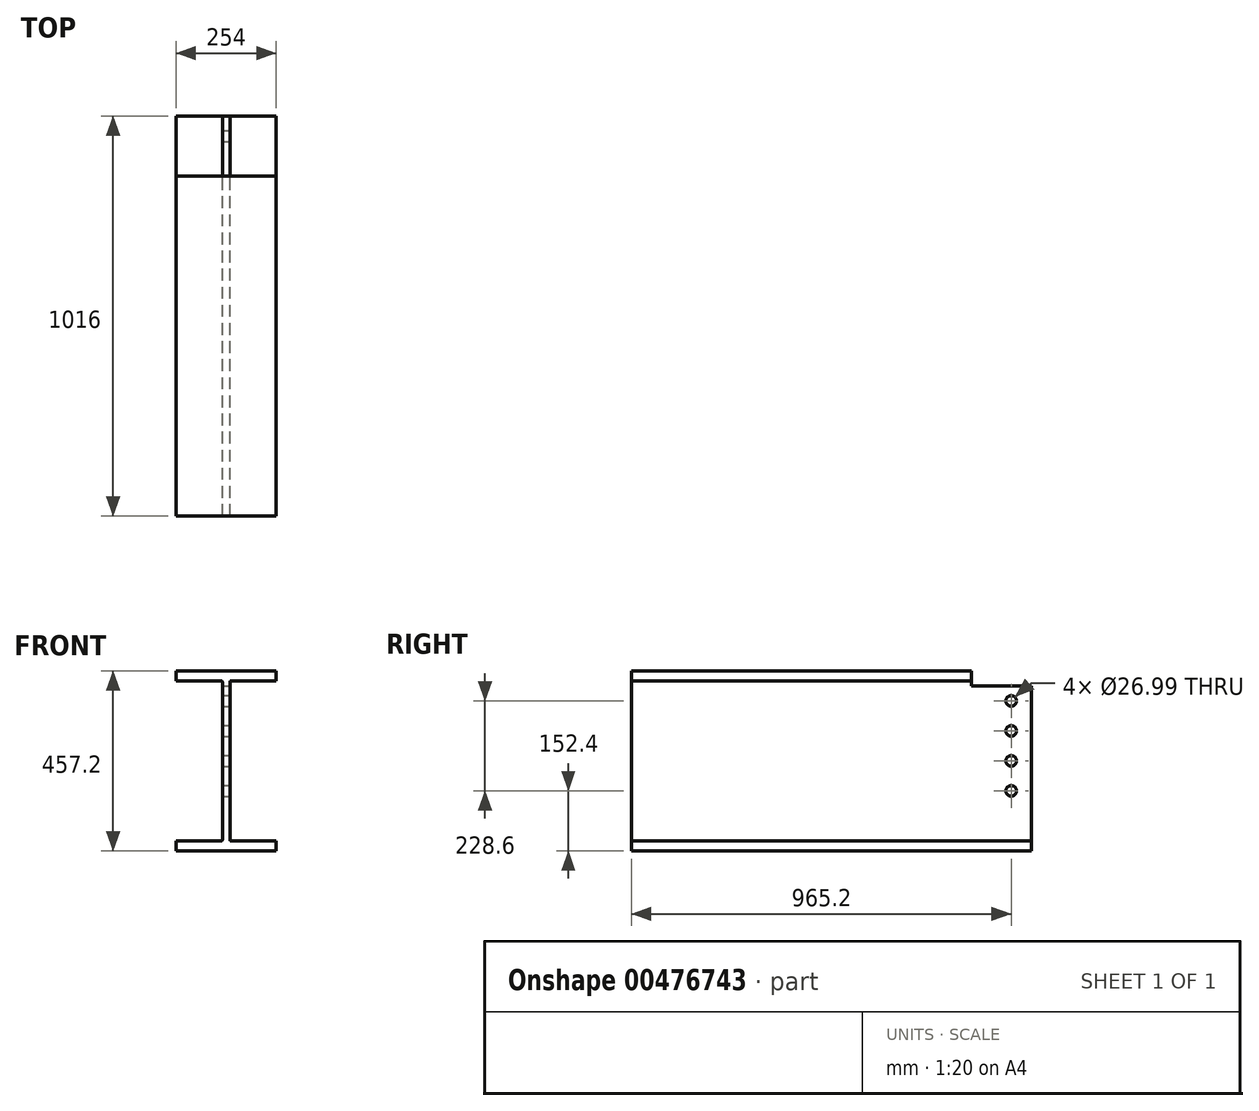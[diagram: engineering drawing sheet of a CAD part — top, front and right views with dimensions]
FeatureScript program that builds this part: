
annotation { "Feature Type Name" : "Feature", "Feature Type Description" : "" }
export const myFeature = defineFeature(function(context is Context, id is Id, definition is map)
    precondition{}
    {
        {
            var Q0;
            Q0=qCreatedBy(makeId("Front.planeOp"),FACE);
            var sketch = newSketch(context, id + "F0", { "sketchPlane" : qUnion([Q0])});
            skLineSegment(sketch, "E0", {"start": v(127, -203.2) * mm, "end": v(12.06, -203.2) * mm});
            skLineSegment(sketch, "E1", {"start": v(9.52, -200.66) * mm, "end": v(9.52, 200.66) * mm});
            skLineSegment(sketch, "E2", {"start": v(12.06, 203.2) * mm, "end": v(127, 203.2) * mm});
            skLineSegment(sketch, "E3", {"start": v(-127, 203.2) * mm, "end": v(-12.06, 203.2) * mm});
            skLineSegment(sketch, "E4", {"start": v(-9.53, 200.66) * mm, "end": v(-9.53, -200.66) * mm});
            skLineSegment(sketch, "E5", {"start": v(-12.06, -203.2) * mm, "end": v(-127, -203.2) * mm});
            skLineSegment(sketch, "E6", {"start": v(0, 0) * mm, "end": v(-9.52, 0) * mm, "construction": true});
            skLineSegment(sketch, "E7", {"start": v(0, 0) * mm, "end": v(9.52, 0) * mm, "construction": true});
            skLineSegment(sketch, "E8", {"start": v(0, 0) * mm, "end": v(0, 228.6) * mm, "construction": true});
            skLineSegment(sketch, "E9", {"start": v(0, 0) * mm, "end": v(0, -228.6) * mm, "construction": true});
            skPoint(sketch, "E10.visualSharp", {"position": v(-9.53, 203.2) * mm});
            skArc(sketch, "E10.filletArc", {"start": v(-9.52, 200.66) * mm, "mid": v(-10.27, 202.46) * mm, "end": v(-12.06, 203.2) * mm});
            skPoint(sketch, "E11.visualSharp", {"position": v(9.53, 203.2) * mm});
            skArc(sketch, "E11.filletArc", {"start": v(12.06, 203.2) * mm, "mid": v(10.27, 202.46) * mm, "end": v(9.52, 200.66) * mm});
            skPoint(sketch, "E12.visualSharp", {"position": v(9.53, -203.2) * mm});
            skArc(sketch, "E12.filletArc", {"start": v(9.52, -200.66) * mm, "mid": v(10.27, -202.46) * mm, "end": v(12.06, -203.2) * mm});
            skPoint(sketch, "E13.visualSharp", {"position": v(-9.53, -203.2) * mm});
            skArc(sketch, "E13.filletArc", {"start": v(-12.06, -203.2) * mm, "mid": v(-10.27, -202.46) * mm, "end": v(-9.52, -200.66) * mm});
            skPoint(sketch, "E14.visualSharp", {"position": v(-127, 228.6) * mm});
            skPoint(sketch, "E15.visualSharp", {"position": v(127, 228.6) * mm});
            skPoint(sketch, "E16.visualSharp", {"position": v(127, 203.2) * mm});
            skPoint(sketch, "E17.visualSharp", {"position": v(127, -228.6) * mm});
            skPoint(sketch, "E18.visualSharp", {"position": v(-127, -203.2) * mm});
            skPoint(sketch, "E19.visualSharp", {"position": v(-127, -228.6) * mm});
            skLineSegment(sketch, "E20", {"start": v(127, -203.2) * mm, "end": v(127, -228.6) * mm});
            skLineSegment(sketch, "E21", {"start": v(-127, -203.2) * mm, "end": v(-127, -228.6) * mm});
            skLineSegment(sketch, "E22", {"start": v(-127, 228.6) * mm, "end": v(-127, 203.2) * mm});
            skLineSegment(sketch, "E23", {"start": v(127, 228.6) * mm, "end": v(127, 203.2) * mm});
            skLineSegment(sketch, "E24", {"start": v(-127, 228.6) * mm, "end": v(127, 228.6) * mm});
            skLineSegment(sketch, "E25", {"start": v(-127, -228.6) * mm, "end": v(127, -228.6) * mm});
            skSolve(sketch);
        }
        {
            var Q0;
            Q0=makeQuery(id+"F0.imprint","IMPRINT",FACE,{"disambiguationData":[TD([[makeQuery(id+"F0.imprint","IMPRINT",EDGE,{"derivedFrom":sQuery(id+"F0.wireOp",EDGE,"E0")}),1.0]])]});
            extrude(context, id + "F1", {"entities" : qUnion([Q0]), "endBound" : BoundingType.SYMMETRIC, "depth" : 1016 * mm});
        }
        {
            var Q0;
            Q0=makeQuery(id+"F1.opExtrude","SWEPT_FACE",FACE,{"disambiguationData":[OSD([sQuery(id+"F0.wireOp",EDGE,"E1")])]});
            var sketch = newSketch(context, id + "F2", { "sketchPlane" : qUnion([Q0])});
            skPoint(sketch, "E26", {"position": v(457.2, 152.4) * mm});
            skPoint(sketch, "E27", {"position": v(457.2, 76.2) * mm});
            skPoint(sketch, "E28", {"position": v(457.2, 0) * mm});
            skPoint(sketch, "E29", {"position": v(457.2, -76.2) * mm});
            skSolve(sketch);
        }
        {
            var Q0;
            Q0=sQuery(id+"F2.wireOp",VERTEX,"E26");
            var Q1;
            Q1=sQuery(id+"F2.wireOp",VERTEX,"E27");
            var Q2;
            Q2=sQuery(id+"F2.wireOp",VERTEX,"E28");
            var Q3;
            Q3=sQuery(id+"F2.wireOp",VERTEX,"E29");
            var Q4;
            Q4=makeQuery(id+"F1.opExtrude","SWEPT_BODY",BODY,{"disambiguationData":[OSD([sQuery(id+"F0.wireOp",EDGE,"E0"),sQuery(id+"F0.wireOp",EDGE,"E1"),sQuery(id+"F0.wireOp",EDGE,"E2"),sQuery(id+"F0.wireOp",EDGE,"E3"),sQuery(id+"F0.wireOp",EDGE,"E4"),sQuery(id+"F0.wireOp",EDGE,"E5"),sQuery(id+"F0.wireOp",EDGE,"E10.filletArc"),sQuery(id+"F0.wireOp",EDGE,"E11.filletArc"),sQuery(id+"F0.wireOp",EDGE,"E12.filletArc"),sQuery(id+"F0.wireOp",EDGE,"E13.filletArc"),sQuery(id+"F0.wireOp",EDGE,"E20"),sQuery(id+"F0.wireOp",EDGE,"E21"),sQuery(id+"F0.wireOp",EDGE,"E22"),sQuery(id+"F0.wireOp",EDGE,"E23"),sQuery(id+"F0.wireOp",EDGE,"E24"),sQuery(id+"F0.wireOp",EDGE,"E25")])]});
            hole(context, id + "F3", {"style" : HoleStyle.SIMPLE, "endStyle" : HoleEndStyle.THROUGH, "holeDiameter" : 26.99 * mm, "isTappedThrough" : true, "tappedDepth" : 12.7 * mm, "tapClearance" : 3, "locations" : qUnion([Q0, Q1, Q2, Q3]), "scope" : qUnion([Q4])});
        }
        {
            var Q0;
            Q0=makeQuery(id+"F1.opExtrude","SWEPT_FACE",FACE,{"disambiguationData":[OSD([sQuery(id+"F0.wireOp",EDGE,"E24")])]});
            var sketch = newSketch(context, id + "F4", { "sketchPlane" : qUnion([Q0])});
            skLineSegment(sketch, "E30.bottom", {"start": v(-127, 508) * mm, "end": v(127, 508) * mm});
            skLineSegment(sketch, "E30.top", {"start": v(-127, 355.6) * mm, "end": v(127, 355.6) * mm});
            skLineSegment(sketch, "E30.left", {"start": v(-127, 508) * mm, "end": v(-127, 355.6) * mm});
            skLineSegment(sketch, "E30.right", {"start": v(127, 508) * mm, "end": v(127, 355.6) * mm});
            skSolve(sketch);
        }
        {
            var Q0;
            Q0=makeQuery(id+"F4.imprint","IMPRINT",FACE,{"disambiguationData":[TD([[makeQuery(id+"F4.imprint","IMPRINT",EDGE,{"derivedFrom":sQuery(id+"F4.wireOp",EDGE,"E30.bottom")}),-1.0]])]});
            extrude(context, id + "F5", {"entities" : qUnion([Q0]), "operationType" : NewBodyOperationType.REMOVE, "oppositeDirection" : true, "depth" : 38.1 * mm});
        }
    });
